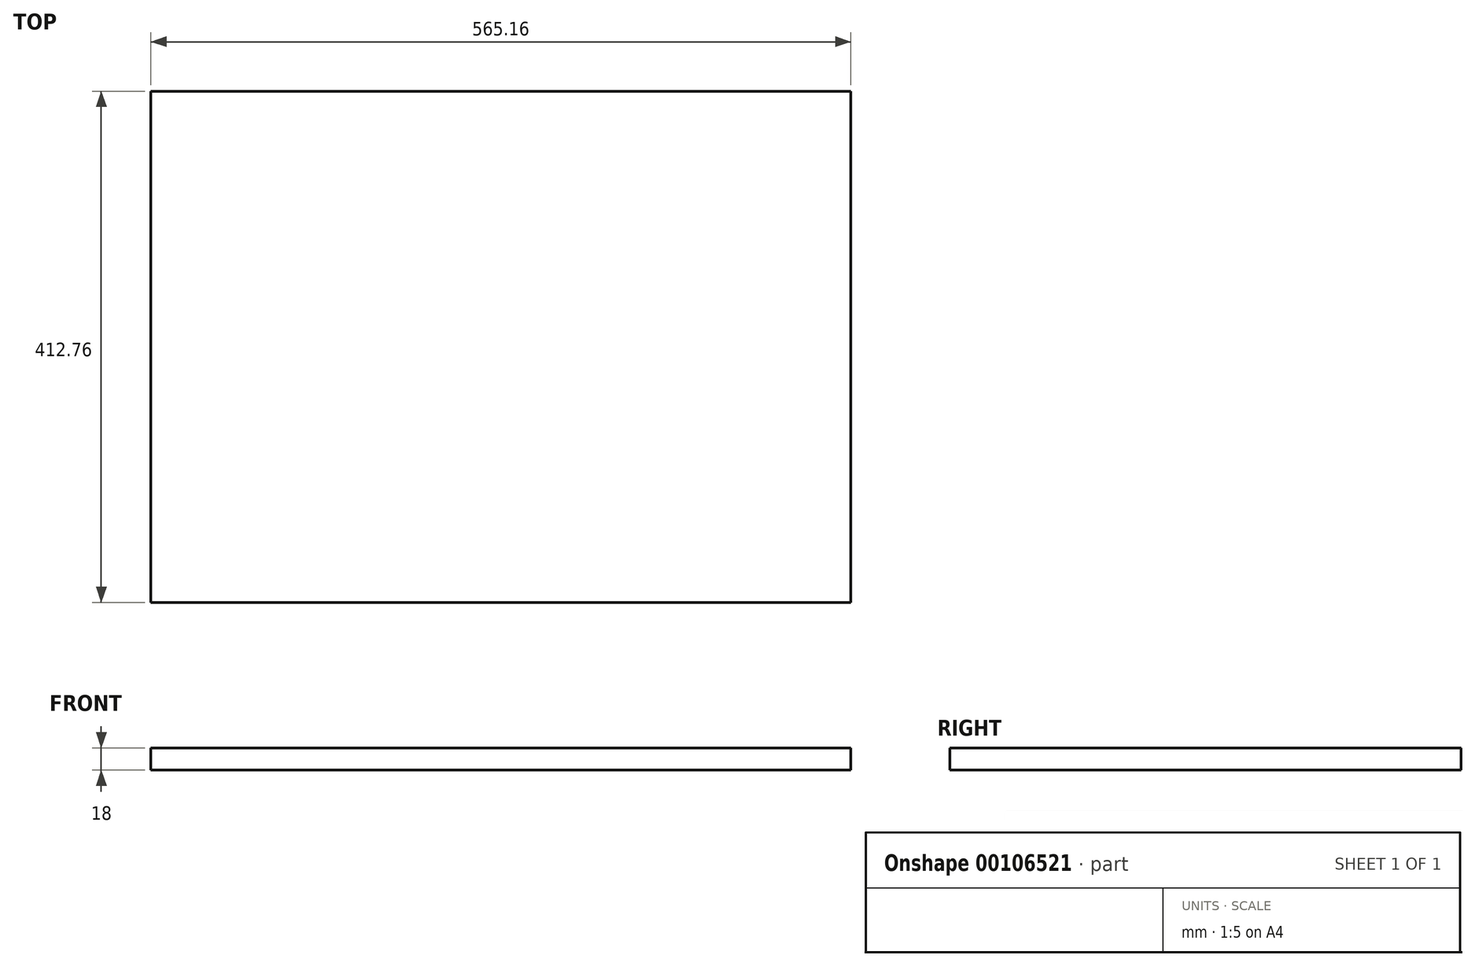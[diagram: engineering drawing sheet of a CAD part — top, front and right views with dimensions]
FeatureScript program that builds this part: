
annotation { "Feature Type Name" : "Feature", "Feature Type Description" : "" }
export const myFeature = defineFeature(function(context is Context, id is Id, definition is map)
    precondition{}
    {
        {
            var Q0;
            Q0=qCreatedBy(makeId("Top.planeOp"),FACE);
            var sketch = newSketch(context, id + "F0", { "sketchPlane" : qUnion([Q0])});
            skLineSegment(sketch, "E0.bottom", {"start": v(282.58, -206.38) * mm, "end": v(-282.57, -206.38) * mm});
            skLineSegment(sketch, "E0.top", {"start": v(282.57, 206.38) * mm, "end": v(-282.57, 206.38) * mm});
            skLineSegment(sketch, "E0.left", {"start": v(282.57, -206.38) * mm, "end": v(282.57, 206.38) * mm});
            skLineSegment(sketch, "E0.right", {"start": v(-282.57, -206.38) * mm, "end": v(-282.57, 206.37) * mm});
            skPoint(sketch, "E0.middle", {"position": v(0, 0) * mm});
            skSolve(sketch);
        }
        {
            var Q0;
            Q0=makeQuery(id+"F0.imprint","IMPRINT",FACE,{"disambiguationData":[TD([[makeQuery(id+"F0.imprint","IMPRINT",EDGE,{"derivedFrom":sQuery(id+"F0.wireOp",EDGE,"E0.bottom")}),-1.0]])]});
            extrude(context, id + "F1", {"entities" : qUnion([Q0]), "depth" : 18 * mm});
        }
    });
